# Revit family: LBRA-6RD
name_source: partatom
category: Lighting Fixtures
units: mm (PartAtom-declared; Revit-internal decimal feet)

## family parameters
Cut with Voids When Loaded = No
Host = Face
Light Source = Yes
OmniClass Number = 23.80.70.11
OmniClass Title = Luminaries for Internal Lighting
Part Type = Normal
Room Calculation Point = No
Round Connector Dimension = Use Diameter
Shared = No

## types (1)
- LBRA-6RD
    Apparent Load = 0 VA
    Backbox = White
    CRI = 90+ CRI
    Certifications = cETLus listed to UL1598
• Can be used in direct contact with insulation
(IC Rated)
• Suitable for wet locations, covered ceiling
• Suitable for use in clothes closets when
installed in accordance to N.E.C. 410.16
• ENERGY STAR® certified
• Meets CA Title 24 High Efficacy (JA8-2019)
requirements
    Color Filter = 16777215
    Default Elevation = 48 "
    Description = The LiteBox® A-Series is a family of retrofit trims that can be used with dedicated LiteBox LED QuickLink housings or installed into existing incandescent recessed housings with a socket adapter accessory.
    Dimming Lamp Color Temperature Shift = <None>
    Features = 4 inch and 6 inch aperture retrofit downlight and wall wash trim
700 or 1000 nominal delivered lumens 
Switchable CCT – 2700K/3000K/3500K/4000K/5000K 
90 CRI standard 
Universal Voltage (120-277V), ideal for commercial applications 
Phase Dimmable to 5% (120V Triac/ELV) 
Retrofit into existing incandescent recessed housings with accessory or use with compatible dedicated LED Quick Link housings
    Glass = White Glass
    Inner Width = 6.1 "
    Lamp = LED Lamp
    Manufacturer = Prescolite Lighting
    Model = LBRA-6RD
    Photometric Web File = LBRA-6RD-T-10LCS9-WH_27K.IES
    Tilt Angle = -90.00°
    URL = https://www.currentlighting.com
    Voltage = 120 V
    Wattage Comments = 11.5W
    Watts = 17 W
    Width = 7.64 "

## geometry (parser evidence)
native form markers: Sweep x2
no freeform markers — native parametric forms only
